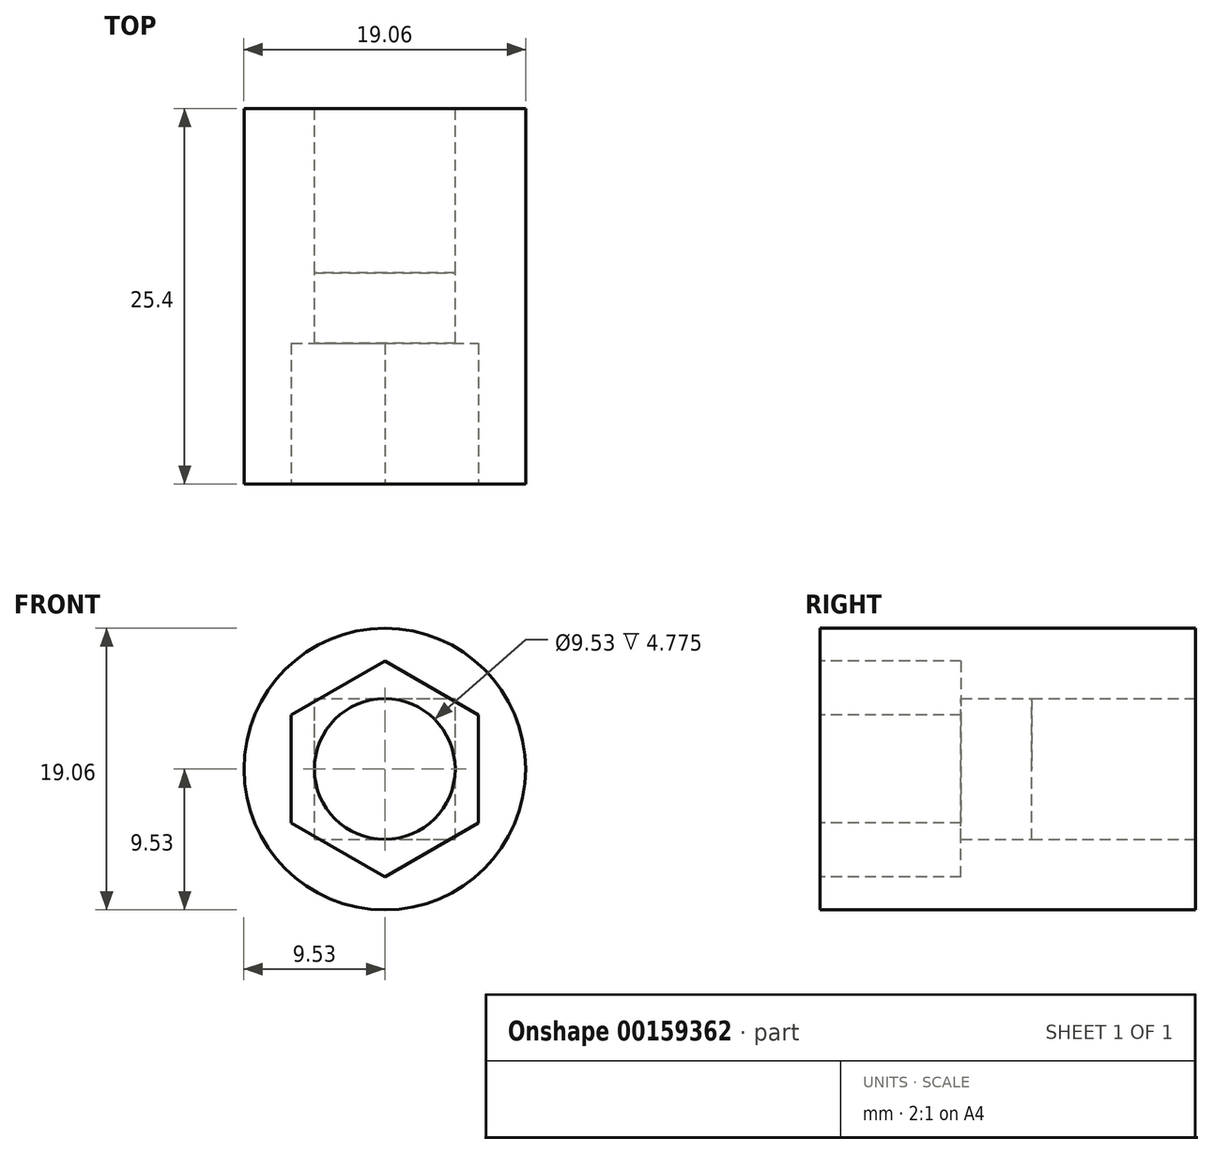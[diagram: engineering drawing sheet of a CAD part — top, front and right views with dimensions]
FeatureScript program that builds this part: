
annotation { "Feature Type Name" : "Feature", "Feature Type Description" : "" }
export const myFeature = defineFeature(function(context is Context, id is Id, definition is map)
    precondition{}
    {
        {
            var Q0;
            Q0=qCreatedBy(makeId("Front.planeOp"),FACE);
            var sketch = newSketch(context, id + "F0", { "sketchPlane" : qUnion([Q0])});
            skCircle(sketch, "E0", {"center": v(0, 0) * mm, "radius": 9.53 * mm});
            skSolve(sketch);
        }
        {
            var Q0;
            Q0 = qSketchRegion(id + "F0", true);
            extrude(context, id + "F1", {"entities" : qUnion([Q0]), "depth" : 25.4 * mm});
        }
        {
            var Q0;
            Q0=makeQuery(id+"F1.opExtrude","CAP_FACE",FACE,{"disambiguationData":[OSD([sQuery(id+"F0.wireOp",EDGE,"E0")])],"isStart":true});
            var sketch = newSketch(context, id + "F2", { "sketchPlane" : qUnion([Q0])});
            skLineSegment(sketch, "E1.bottom", {"start": v(4.76, -4.76) * mm, "end": v(-4.76, -4.76) * mm});
            skLineSegment(sketch, "E1.top", {"start": v(4.76, 4.76) * mm, "end": v(-4.76, 4.76) * mm});
            skLineSegment(sketch, "E1.left", {"start": v(4.76, -4.76) * mm, "end": v(4.76, 4.76) * mm});
            skLineSegment(sketch, "E1.right", {"start": v(-4.76, -4.76) * mm, "end": v(-4.76, 4.76) * mm});
            skPoint(sketch, "E1.middle", {"position": v(0, 0) * mm});
            skSolve(sketch);
        }
        {
            var Q0;
            Q0=makeQuery(id+"F1.opExtrude","CAP_FACE",FACE,{"disambiguationData":[OSD([sQuery(id+"F0.wireOp",EDGE,"E0")])],"isStart":true});
            var sketch = newSketch(context, id + "F3", { "sketchPlane" : qUnion([Q0])});
            skCircle(sketch, "E2", {"center": v(0, 0) * mm, "radius": 4.76 * mm});
            skSolve(sketch);
        }
        {
            var Q0;
            Q0 = qSketchRegion(id + "F3", true);
            extrude(context, id + "F4", {"entities" : qUnion([Q0]), "operationType" : NewBodyOperationType.REMOVE, "oppositeDirection" : true, "depth" : 25.4 * mm});
        }
        {
            var Q0;
            Q0 = qSketchRegion(id + "F2", true);
            extrude(context, id + "F5", {"entities" : qUnion([Q0]), "operationType" : NewBodyOperationType.REMOVE, "oppositeDirection" : true, "depth" : 11.1 * mm});
        }
        {
            var Q0;
            Q0=makeQuery(id+"F1.opExtrude","CAP_FACE",FACE,{"disambiguationData":[OSD([sQuery(id+"F0.wireOp",EDGE,"E0")])],"isStart":false});
            var sketch = newSketch(context, id + "F6", { "sketchPlane" : qUnion([Q0])});
            skCircle(sketch, "E3.cCircle", {"center": v(0, 0) * mm, "radius": 6.32 * mm, "construction": true});
            skLineSegment(sketch, "E3.0", {"start": v(6.32, 3.65) * mm, "end": v(6.32, -3.65) * mm});
            skLineSegment(sketch, "E3.1", {"start": v(6.32, -3.65) * mm, "end": v(0, -7.3) * mm});
            skLineSegment(sketch, "E3.2", {"start": v(0, -7.3) * mm, "end": v(-6.32, -3.65) * mm});
            skLineSegment(sketch, "E3.3", {"start": v(-6.32, -3.65) * mm, "end": v(-6.32, 3.65) * mm});
            skLineSegment(sketch, "E3.4", {"start": v(-6.32, 3.65) * mm, "end": v(0, 7.3) * mm});
            skLineSegment(sketch, "E3.5", {"start": v(0, 7.3) * mm, "end": v(6.32, 3.65) * mm});
            skPoint(sketch, "E3.0.midPoint", {"position": v(6.32, 0) * mm});
            skSolve(sketch);
        }
        {
            var Q0;
            Q0 = qSketchRegion(id + "F6", true);
            extrude(context, id + "F7", {"entities" : qUnion([Q0]), "operationType" : NewBodyOperationType.REMOVE, "oppositeDirection" : true, "depth" : 9.52 * mm});
        }
    });
